# Revit family: EWB
name_source: partatom
category: Mechanical Equipment
units: mm (PartAtom-declared; Revit-internal decimal feet)

## family parameters
Always vertical = Yes
Cut with Voids When Loaded = No
Part Type = Normal
Room Calculation Point = No
Round Connector Dimension = Use Diameter
Shared = No
Work Plane-Based = No

## types (8) — shared parameters
-D = -3"
.125 = 1/8"
.5" = 1/2"
0 = 0"
1" = 1"
1.5 = 1 1/2"
2" = 2"
2' = 24"
3" = 3"
4" = 4"
4'6" = 54"
9" = 9"
E = 3"
E/2 = 1 1/2"
Manufacturer = Loren Cook Company
Model = EWB
Type Comments = Wall Exhaust Fan Extruded Aluminum Propeller Belt Drive
URL = www.lorencook.com
WH_ANGLE = 130.00°
WH_ANGLE_2 = 92.00°

## per-type parameters (varying)
- 24_EWB: (A/2)-1"=17 27/32"; (A/2)-C-.5"=10 31/32"; (D_SUP/2)-(C/2)-.125"=11 9/16"; (SIZE/2)-.25"=14 11/16"; -((A/2)-C-.5")=-10 31/32"; -((SIZE/2)-.25")=-14 11/16"; -B=-20"; -B+1"=-18"; -C/2=-3 5/16"; -WC_D=-18 11/16"; -WG_A=-20 9/16"; -WH_B/2=-20"; A=36 3/16"; A/2=18 3/32"; A/3.5=10 11/32"; A/7=5 5/32"; B=20"; B/2=10"; B/4=5"; C=6 5/8"; C/2=3 5/16"; D=30"; D/2=15"; MOTOR=3"; SIZE=29 7/8"; SIZE/2=14 15/16"; WC_A=36 1/4"; WC_B=39 9/16"; WC_C=34 7/16"; WG_B=37"; WG_D=12 9/16"; WH_A=27 1/8"; WH_B=40"; WH_B/2=20"
- 30_EWB: (A/2)-1"=20 27/32"; (A/2)-C-.5"=13 27/32"; (D_SUP/2)-(C/2)-.125"=14 1/2"; (SIZE/2)-.25"=17 11/16"; -((A/2)-C-.5")=-13 27/32"; -((SIZE/2)-.25")=-17 11/16"; -B=-21"; -B+1"=-19"; -C/2=-3 3/8"; -WC_D=-19 7/16"; -WG_A=-20 9/16"; -WH_B/2=-23"; A=42 3/16"; A/2=21 3/32"; A/3.5=12 1/16"; A/7=6 1/32"; B=21"; B/2=10 1/2"; B/4=5 1/4"; C=6 3/4"; C/2=3 3/8"; D=36"; D/2=18"; MOTOR=3 19/32"; SIZE=35 7/8"; SIZE/2=17 15/16"; WC_A=42 1/4"; WC_B=45 9/16"; WC_C=40 1/2"; WG_B=43"; WG_D=12 9/16"; WH_A=35 11/16"; WH_B=46"; WH_B/2=23"
- 36_EWB: (A/2)-1"=23 27/32"; (A/2)-C-.5"=16 11/32"; (D_SUP/2)-(C/2)-.125"=17 1/4"; (SIZE/2)-.25"=20 11/16"; -((A/2)-C-.5")=-16 11/32"; -((SIZE/2)-.25")=-20 11/16"; -B=-21"; -B+1"=-19"; -C/2=-3 5/8"; -WC_D=-19 7/16"; -WG_A=-25 9/16"; -WH_B/2=-26"; A=48 3/16"; A/2=24 3/32"; A/3.5=13 25/32"; A/7=6 7/8"; B=21"; B/2=10 1/2"; B/4=5 1/4"; C=7 1/4"; C/2=3 5/8"; D=42"; D/2=21"; MOTOR=4 3/16"; SIZE=41 7/8"; SIZE/2=20 15/16"; WC_A=48 1/4"; WC_B=51 5/8"; WC_C=46 1/2"; WG_B=49"; WG_D=12 9/16"; WH_A=39 15/16"; WH_B=52"; WH_B/2=26"
- 42_EWB: (A/2)-1"=26 27/32"; (A/2)-C-.5"=18 17/32"; (D_SUP/2)-(C/2)-.125"=19 27/32"; (SIZE/2)-.25"=23 11/16"; -((A/2)-C-.5")=-18 17/32"; -((SIZE/2)-.25")=-23 11/16"; -B=-21"; -B+1"=-19"; -C/2=-4 1/32"; -WC_D=-19 11/16"; -WG_A=-28 7/16"; -WH_B/2=-29"; A=54 3/16"; A/2=27 3/32"; A/3.5=15 15/32"; A/7=7 3/4"; B=21"; B/2=10 1/2"; B/4=5 1/4"; C=8 1/16"; C/2=4 1/32"; D=48"; D/2=24"; MOTOR=4 13/16"; SIZE=47 7/8"; SIZE/2=23 15/16"; WC_A=54 1/4"; WC_B=57 5/8"; WC_C=52 1/2"; WG_B=55"; WG_D=13 7/16"; WH_A=44 3/16"; WH_B=58"; WH_B/2=29"
- 48_EWB: (A/2)-1"=29 27/32"; (A/2)-C-.5"=21 17/32"; (D_SUP/2)-(C/2)-.125"=22 27/32"; (SIZE/2)-.25"=26 11/16"; -((A/2)-C-.5")=-21 17/32"; -((SIZE/2)-.25")=-26 11/16"; -B=-24"; -B+1"=-22"; -C/2=-4 1/32"; -WC_D=-19 11/16"; -WG_A=-28 7/16"; -WH_B/2=-32"; A=60 3/16"; A/2=30 3/32"; A/3.5=17 3/16"; A/7=8 19/32"; B=24"; B/2=12"; B/4=6"; C=8 1/16"; C/2=4 1/32"; D=54"; D/2=27"; MOTOR=5 13/32"; SIZE=53 7/8"; SIZE/2=26 15/16"; WC_A=60 1/4"; WC_B=63 11/16"; WC_C=58 9/16"; WG_B=61"; WG_D=13 7/16"; WH_A=48 7/16"; WH_B=64"; WH_B/2=32"
- 54_EWB: (A/2)-1"=32 27/32"; (A/2)-C-.5"=24 17/32"; (D_SUP/2)-(C/2)-.125"=25 27/32"; (SIZE/2)-.25"=29 11/16"; -((A/2)-C-.5")=-24 17/32"; -((SIZE/2)-.25")=-29 11/16"; -B=-27"; -B+1"=-25"; -C/2=-4 1/32"; -WC_D=-19 11/16"; -WG_A=-28 7/16"; -WH_B/2=-35"; A=66 3/16"; A/2=33 3/32"; A/3.5=18 29/32"; A/7=9 15/32"; B=27"; B/2=13 1/2"; B/4=6 3/4"; C=8 1/16"; C/2=4 1/32"; D=60"; D/2=30"; MOTOR=6"; SIZE=59 7/8"; SIZE/2=29 15/16"; WC_A=66 1/4"; WC_B=69 11/16"; WC_C=64 9/16"; WG_B=67"; WG_D=13 7/16"; WH_A=52 5/8"; WH_B=70"; WH_B/2=35"
- 60_EWB: (A/2)-1"=35 27/32"; (A/2)-C-.5"=27 17/32"; (D_SUP/2)-(C/2)-.125"=28 27/32"; (SIZE/2)-.25"=32 11/16"; -((A/2)-C-.5")=-27 17/32"; -((SIZE/2)-.25")=-32 11/16"; -B=-27"; -B+1"=-25"; -C/2=-4 1/32"; -WC_D=-19 11/16"; -WG_A=-28 7/16"; -WH_B/2=-38"; A=72 3/16"; A/2=36 3/32"; A/3.5=20 5/8"; A/7=10 5/16"; B=27"; B/2=13 1/2"; B/4=6 3/4"; C=8 1/16"; C/2=4 1/32"; D=66"; D/2=33"; MOTOR=6 19/32"; SIZE=65 7/8"; SIZE/2=32 15/16"; WC_A=72 1/4"; WC_B=75 11/16"; WC_C=70 9/16"; WG_B=73"; WG_D=13 7/16"; WH_A=56 13/16"; WH_B=76"; WH_B/2=38"
- 72_EWB: (A/2)-1"=41 27/32"; (A/2)-C-.5"=32 11/32"; (D_SUP/2)-(C/2)-.125"=34 3/8"; (SIZE/2)-.25"=38 13/16"; -((A/2)-C-.5")=-32 11/32"; -((SIZE/2)-.25")=-38 13/16"; -B=-27"; -B+1"=-25"; -C/2=-4 5/8"; -WC_D=-19 11/16"; -WG_A=-30 9/16"; -WH_B/2=-44"; A=84 3/16"; A/2=42 3/32"; A/3.5=24 1/16"; A/7=12 1/32"; B=27"; B/2=13 1/2"; B/4=6 3/4"; C=9 1/4"; C/2=4 5/8"; D=78 1/4"; D/2=39 1/8"; MOTOR=7 13/16"; SIZE=78 1/8"; SIZE/2=39 1/16"; WC_A=84 1/4"; WC_B=87 11/16"; WC_C=82 9/16"; WG_B=85"; WG_D=13 7/16"; WH_A=65 7/16"; WH_B=88"; WH_B/2=44"

## geometry (parser evidence)
native form markers: Sweep x2
no freeform markers — native parametric forms only
